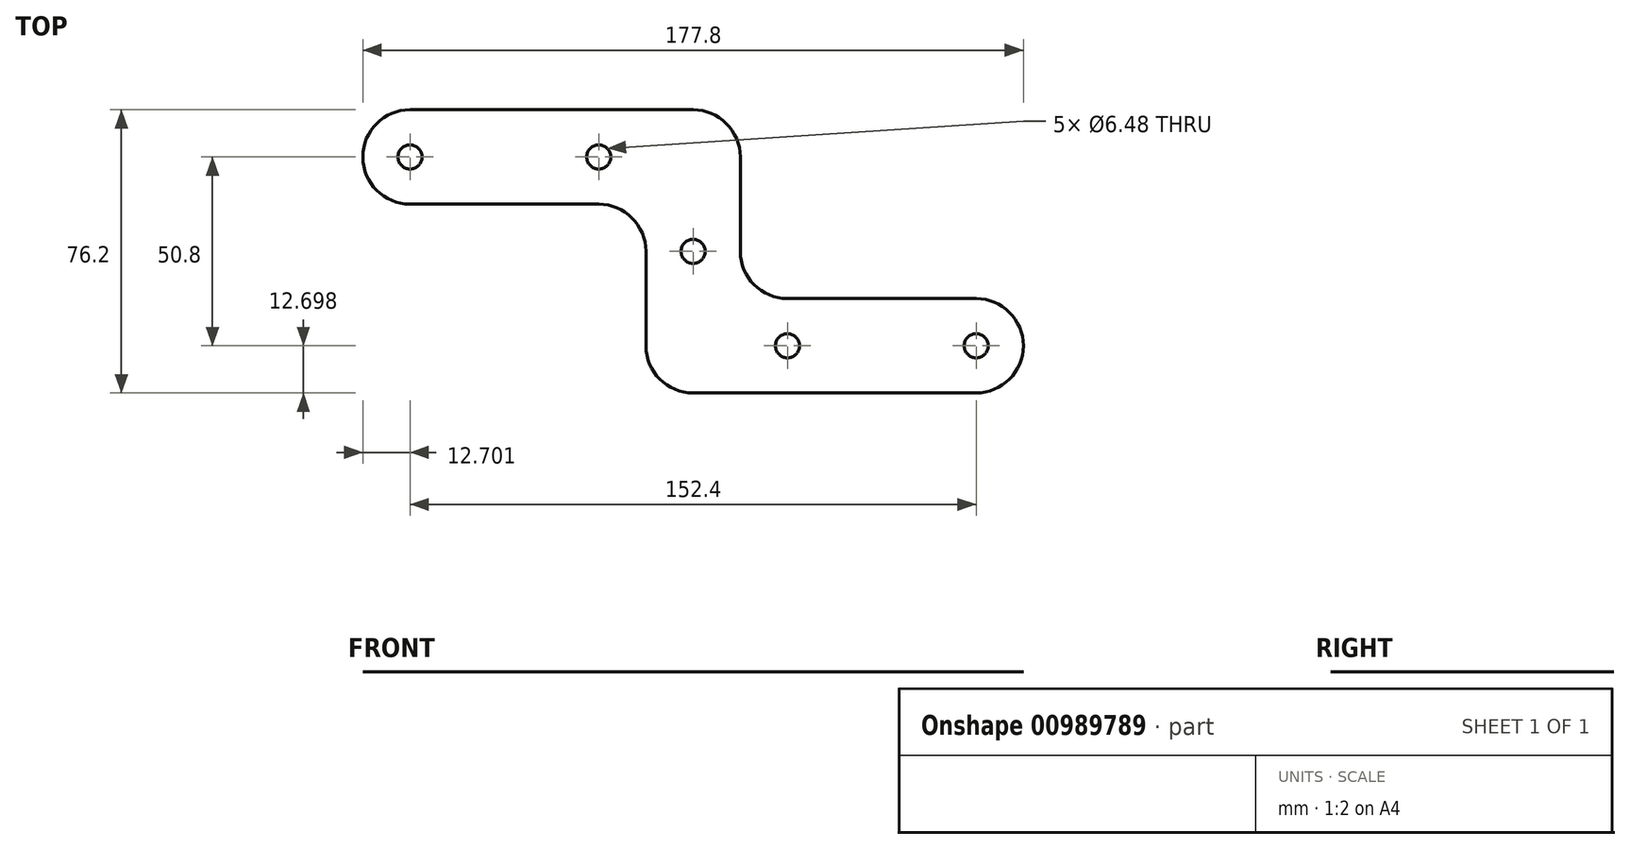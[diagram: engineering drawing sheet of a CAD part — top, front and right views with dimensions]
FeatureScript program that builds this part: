
annotation { "Feature Type Name" : "Feature", "Feature Type Description" : "" }
export const myFeature = defineFeature(function(context is Context, id is Id, definition is map)
    precondition{}
    {
        {
            var Q0;
            Q0=qCreatedBy(makeId("Top.planeOp"),FACE);
            var sketch = newSketch(context, id + "F0", { "sketchPlane" : qUnion([Q0])});
            skLineSegment(sketch, "E0.bottom", {"start": v(-35.07, 44.49) * mm, "end": v(41.13, 44.49) * mm});
            skLineSegment(sketch, "E0.top", {"start": v(-35.07, 19.09) * mm, "end": v(28.43, 19.09) * mm});
            skLineSegment(sketch, "E0.left", {"start": v(-47.77, 31.79) * mm, "end": v(-47.77, 31.79) * mm});
            skLineSegment(sketch, "E0.right", {"start": v(53.83, 31.79) * mm, "end": v(53.83, 19.09) * mm});
            skLineSegment(sketch, "E1.bottom", {"start": v(53.83, -6.31) * mm, "end": v(117.33, -6.31) * mm});
            skLineSegment(sketch, "E1.top", {"start": v(41.13, -31.71) * mm, "end": v(117.33, -31.71) * mm});
            skLineSegment(sketch, "E1.left", {"start": v(28.43, -6.31) * mm, "end": v(28.43, -19.01) * mm});
            skLineSegment(sketch, "E1.right", {"start": v(130.03, -19.01) * mm, "end": v(130.03, -19.01) * mm});
            skLineSegment(sketch, "E2.left", {"start": v(28.43, 19.09) * mm, "end": v(28.43, -6.31) * mm});
            skLineSegment(sketch, "E2.right", {"start": v(53.83, 19.09) * mm, "end": v(53.83, -6.31) * mm});
            skPoint(sketch, "E3.visualSharp", {"position": v(-47.77, 44.49) * mm});
            skArc(sketch, "E3.filletArc", {"start": v(-35.07, 44.49) * mm, "mid": v(-44.05, 40.77) * mm, "end": v(-47.77, 31.79) * mm});
            skPoint(sketch, "E4.visualSharp", {"position": v(-47.77, 19.09) * mm});
            skArc(sketch, "E4.filletArc", {"start": v(-47.77, 31.79) * mm, "mid": v(-44.05, 22.8) * mm, "end": v(-35.07, 19.09) * mm});
            skPoint(sketch, "E5.visualSharp", {"position": v(53.83, 44.49) * mm});
            skArc(sketch, "E5.filletArc", {"start": v(53.83, 31.79) * mm, "mid": v(50.11, 40.77) * mm, "end": v(41.13, 44.49) * mm});
            skPoint(sketch, "E6.visualSharp", {"position": v(28.43, -31.71) * mm});
            skArc(sketch, "E6.filletArc", {"start": v(28.43, -19.01) * mm, "mid": v(32.15, -28) * mm, "end": v(41.13, -31.71) * mm});
            skPoint(sketch, "E7.visualSharp", {"position": v(130.03, -6.31) * mm});
            skArc(sketch, "E7.filletArc", {"start": v(130.03, -19.01) * mm, "mid": v(126.31, -10.03) * mm, "end": v(117.33, -6.31) * mm});
            skPoint(sketch, "E8.visualSharp", {"position": v(130.03, -31.71) * mm});
            skArc(sketch, "E8.filletArc", {"start": v(117.33, -31.71) * mm, "mid": v(126.31, -28) * mm, "end": v(130.03, -19.01) * mm});
            skLineSegment(sketch, "E9", {"start": v(53.83, 19.09) * mm, "end": v(28.43, -6.31) * mm, "construction": true});
            skCircle(sketch, "E10", {"center": v(41.13, 6.39) * mm, "radius": 3.24 * mm});
            skLineSegment(sketch, "E11", {"start": v(-47.77, 31.79) * mm, "end": v(-35.07, 31.79) * mm, "construction": true});
            skLineSegment(sketch, "E12", {"start": v(53.83, 31.79) * mm, "end": v(15.73, 31.79) * mm, "construction": true});
            skCircle(sketch, "E13", {"center": v(-35.07, 31.79) * mm, "radius": 3.24 * mm});
            skCircle(sketch, "E14", {"center": v(15.73, 31.79) * mm, "radius": 3.24 * mm});
            skCircle(sketch, "E15", {"center": v(66.53, -19.01) * mm, "radius": 3.24 * mm});
            skCircle(sketch, "E16", {"center": v(117.33, -19.01) * mm, "radius": 3.24 * mm});
            skLineSegment(sketch, "E17", {"start": v(130.03, -19.01) * mm, "end": v(117.33, -19.01) * mm, "construction": true});
            skSolve(sketch);
        }
        {
            var Q0;
            Q0 = qSketchRegion(id + "F0", true);
            extrude(context, id + "F1", {"entities" : qUnion([Q0]), "flatOperationType" : FlatOperationType.REMOVE, "depth" : 1 / 406.4 * mm, "offsetDistance" : 25.4 * mm, "domain" : OperationDomain.MODEL});
        }
        {
            var Q0;
            Q0=makeQuery(id+"F1.opExtrude","SWEPT_EDGE",EDGE,{"disambiguationData":[OSD([sQuery(id+"F0.wireOp",EDGE,"E0.top"),sQuery(id+"F0.wireOp",EDGE,"E2.left")])]});
            var Q1;
            Q1=makeQuery(id+"F1.opExtrude","SWEPT_EDGE",EDGE,{"disambiguationData":[OSD([sQuery(id+"F0.wireOp",EDGE,"E1.bottom"),sQuery(id+"F0.wireOp",EDGE,"E2.right")])]});
            fillet(context, id + "F2", {"entities" : qUnion([Q0, Q1]), "radius" : 12.7 * mm, "tangentPropagation" : true, "allowEdgeOverflow" : false});
        }
    });
